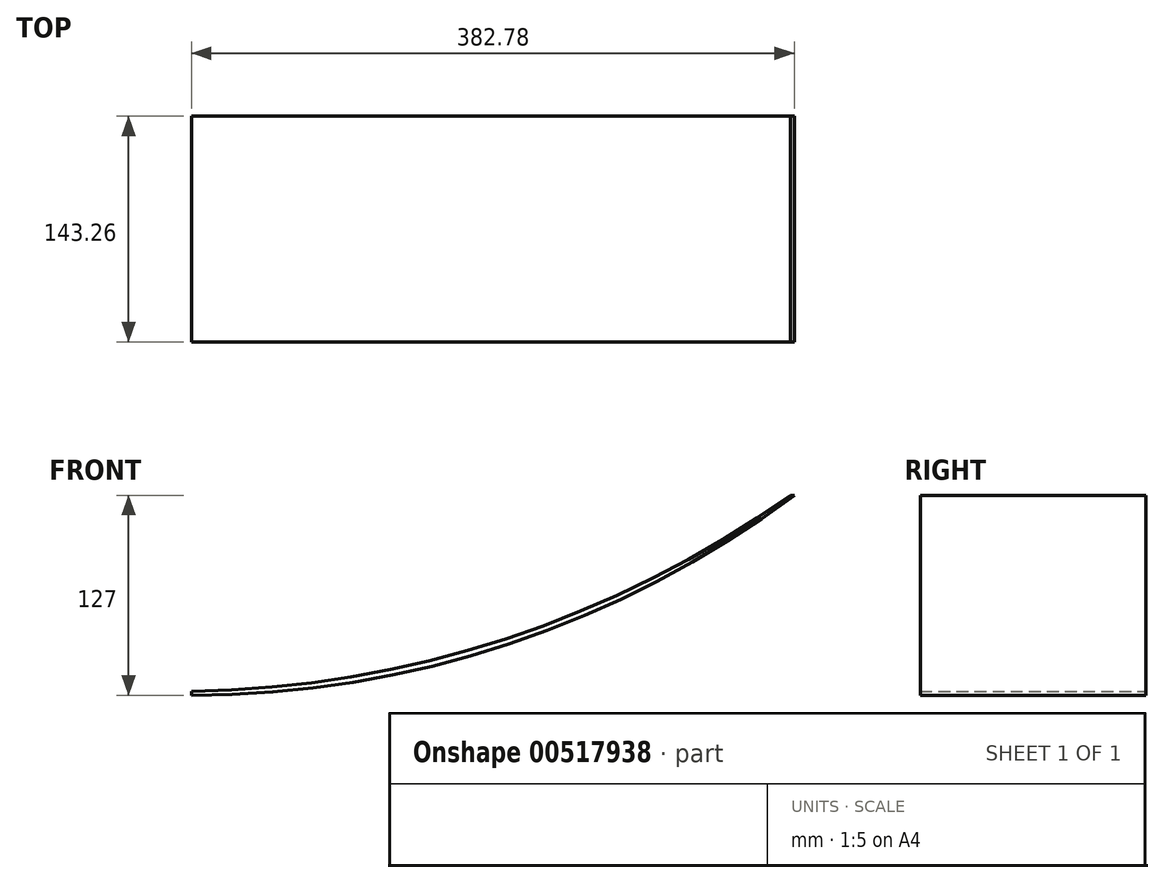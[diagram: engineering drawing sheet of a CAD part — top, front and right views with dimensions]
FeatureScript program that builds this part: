
annotation { "Feature Type Name" : "Feature", "Feature Type Description" : "" }
export const myFeature = defineFeature(function(context is Context, id is Id, definition is map)
    precondition{}
    {
        {
            var Q0;
            Q0=qCreatedBy(makeId("Front.planeOp"),FACE);
            var sketch = newSketch(context, id + "F0", { "sketchPlane" : qUnion([Q0])});
            skArc(sketch, "E0", {"start": v(-290.22, 0) * mm, "mid": v(-88.57, 32.58) * mm, "end": v(92.56, 127) * mm});
            skLineSegment(sketch, "E1", {"start": v(92.56, 127) * mm, "end": v(90.02, 127) * mm});
            skLineSegment(sketch, "E2", {"start": v(-290.22, 0) * mm, "end": v(-290.22, 2.54) * mm});
            skArc(sketch, "E3", {"start": v(-290.22, 2.54) * mm, "mid": v(-90.64, 35.86) * mm, "end": v(90.02, 127) * mm});
            skSolve(sketch);
        }
        {
            var Q0;
            Q0=makeQuery(id+"F0.imprint","IMPRINT",FACE,{"disambiguationData":[TD([[makeQuery(id+"F0.imprint","IMPRINT",EDGE,{"derivedFrom":sQuery(id+"F0.wireOp",EDGE,"E0")}),1.0]])]});
            extrude(context, id + "F1", {"entities" : qUnion([Q0]), "depth" : 143.26 * mm, "offsetDistance" : 25.4 * mm});
        }
    });
